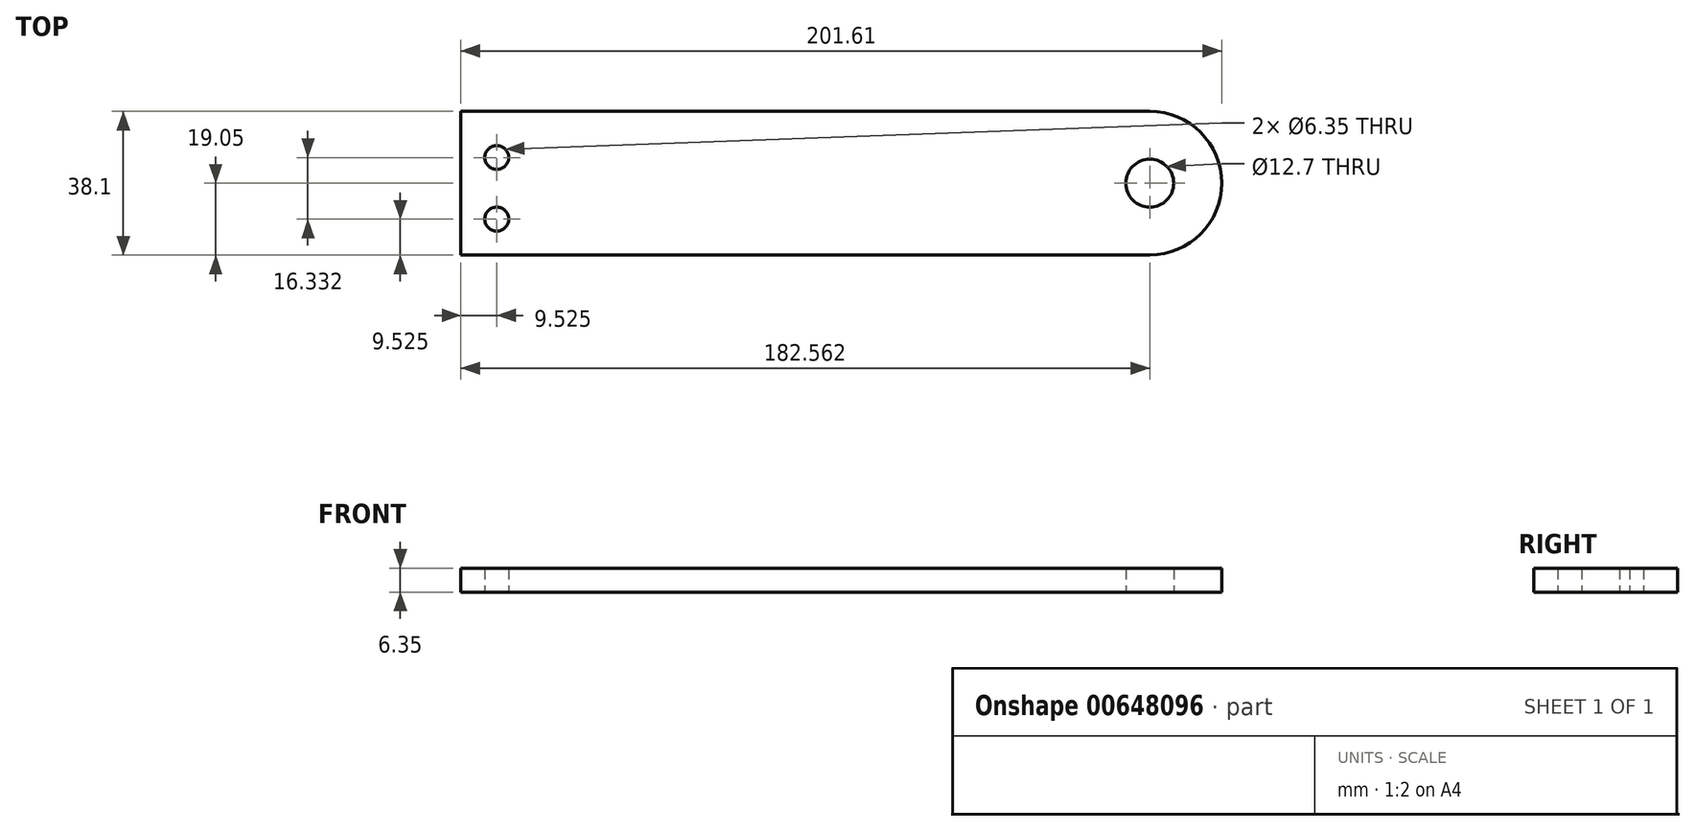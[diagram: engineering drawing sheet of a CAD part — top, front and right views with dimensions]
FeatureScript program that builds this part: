
annotation { "Feature Type Name" : "Feature", "Feature Type Description" : "" }
export const myFeature = defineFeature(function(context is Context, id is Id, definition is map)
    precondition{}
    {
        {
            var Q0;
            Q0=qCreatedBy(makeId("Top.planeOp"),FACE);
            var sketch = newSketch(context, id + "F0", { "sketchPlane" : qUnion([Q0])});
            skLineSegment(sketch, "E0.bottom", {"start": v(81.07, -19.05) * mm, "end": v(-101.5, -19.05) * mm});
            skLineSegment(sketch, "E0.right", {"start": v(-101.5, -19.05) * mm, "end": v(-101.5, 19.05) * mm});
            skPoint(sketch, "E0.middle", {"position": v(0, 0) * mm});
            skCircle(sketch, "E1", {"center": v(81.07, 0) * mm, "radius": 6.35 * mm});
            skCircle(sketch, "E2", {"center": v(-91.97, -9.52) * mm, "radius": 3.18 * mm});
            skCircle(sketch, "E3", {"center": v(-91.97, 6.8) * mm, "radius": 3.18 * mm});
            skLineSegment(sketch, "E4", {"start": v(-101.5, 19.05) * mm, "end": v(81.07, 19.05) * mm});
            skArc(sketch, "E5", {"start": v(81.07, -19.05) * mm, "mid": v(100.12, 0) * mm, "end": v(81.07, 19.05) * mm});
            skSolve(sketch);
        }
        {
            var Q0;
            Q0 = qSketchRegion(id + "F0", true);
            extrude(context, id + "F1", {"entities" : qUnion([Q0]), "depth" : 6.35 * mm, "offsetDistance" : 25.4 * mm});
        }
    });
